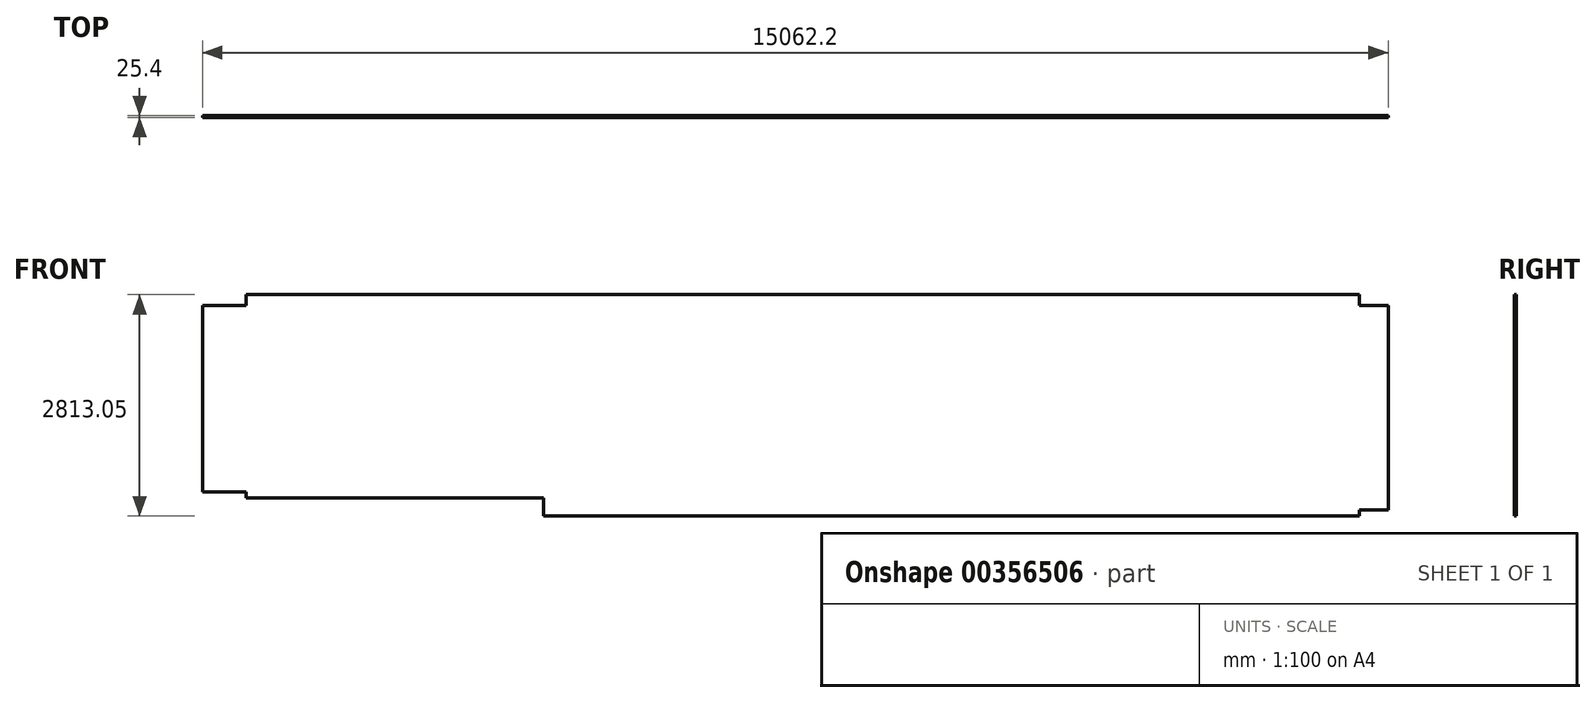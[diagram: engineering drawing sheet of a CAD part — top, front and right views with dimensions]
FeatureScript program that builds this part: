
annotation { "Feature Type Name" : "Feature", "Feature Type Description" : "" }
export const myFeature = defineFeature(function(context is Context, id is Id, definition is map)
    precondition{}
    {
        {
            var Q0;
            Q0=qCreatedBy(makeId("Front.planeOp"),FACE);
            var sketch = newSketch(context, id + "F0", { "sketchPlane" : qUnion([Q0])});
            skLineSegment(sketch, "E0.bottom", {"start": v(4330.7, 0) * mm, "end": v(14693.9, 0) * mm});
            skLineSegment(sketch, "E0.top", {"start": v(552.45, 2813.05) * mm, "end": v(14693.9, 2813.05) * mm});
            skLineSegment(sketch, "E0.left", {"start": v(0, 304.8) * mm, "end": v(0, 2673.35) * mm});
            skLineSegment(sketch, "E0.right", {"start": v(15062.2, 76.2) * mm, "end": v(15062.2, 2673.35) * mm});
            skLineSegment(sketch, "E1", {"start": v(0, 2673.35) * mm, "end": v(552.45, 2673.35) * mm});
            skLineSegment(sketch, "E2", {"start": v(552.45, 2673.35) * mm, "end": v(552.45, 2813.05) * mm});
            skLineSegment(sketch, "E3", {"start": v(4330.7, 0) * mm, "end": v(4330.7, 228.6) * mm});
            skLineSegment(sketch, "E4", {"start": v(4330.7, 228.6) * mm, "end": v(552.45, 228.6) * mm});
            skLineSegment(sketch, "E5", {"start": v(552.45, 228.6) * mm, "end": v(552.45, 304.8) * mm});
            skLineSegment(sketch, "E6", {"start": v(552.45, 304.8) * mm, "end": v(0, 304.8) * mm});
            skLineSegment(sketch, "E7", {"start": v(14693.9, 2813.05) * mm, "end": v(14693.9, 2673.35) * mm});
            skLineSegment(sketch, "E8", {"start": v(14693.9, 2673.35) * mm, "end": v(15062.2, 2673.35) * mm});
            skLineSegment(sketch, "E9", {"start": v(15062.2, 76.2) * mm, "end": v(14693.9, 76.2) * mm});
            skLineSegment(sketch, "E10", {"start": v(14693.9, 76.2) * mm, "end": v(14693.9, 0) * mm});
            skSolve(sketch);
        }
        {
            var Q0;
            Q0 = qSketchRegion(id + "F0", true);
            extrude(context, id + "F1", {"entities" : qUnion([Q0]), "depth" : 25.4 * mm});
        }
    });
